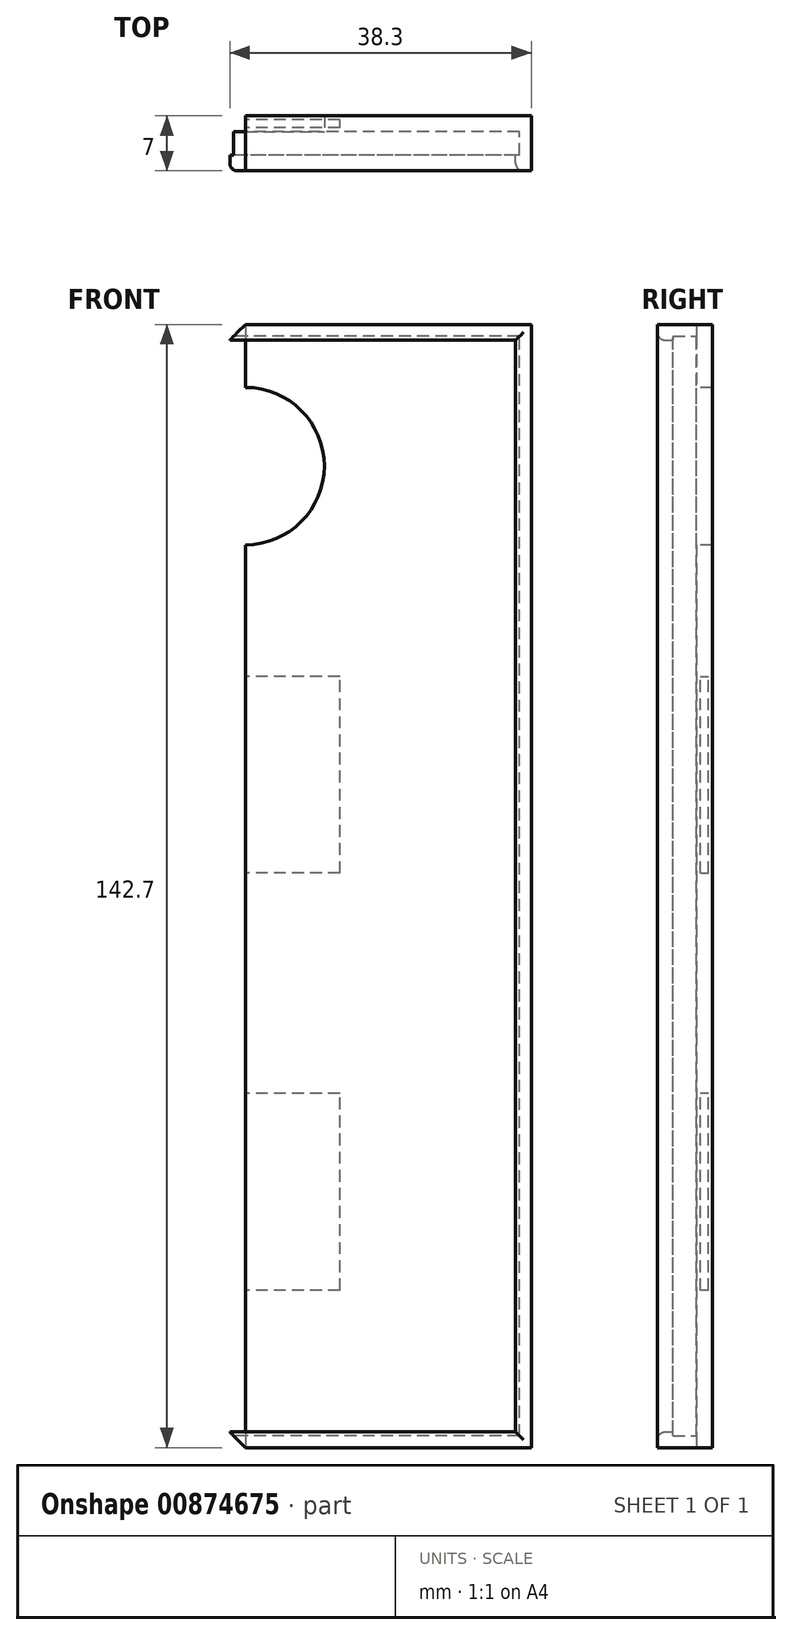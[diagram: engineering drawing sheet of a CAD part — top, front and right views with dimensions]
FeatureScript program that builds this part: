
annotation { "Feature Type Name" : "Feature", "Feature Type Description" : "" }
export const myFeature = defineFeature(function(context is Context, id is Id, definition is map)
    precondition{}
    {
        {
            var Q0;
            Q0=qCreatedBy(makeId("Right.planeOp"),FACE);
            var sketch = newSketch(context, id + "F0", { "sketchPlane" : qUnion([Q0])});
            skLineSegment(sketch, "E0.bottom", {"start": v(0.5, 132.36) * mm, "end": v(-1.5, 132.36) * mm});
            skLineSegment(sketch, "E0.top", {"start": v(0.5, -10.34) * mm, "end": v(-1.5, -10.34) * mm});
            skLineSegment(sketch, "E0.left", {"start": v(0.5, 132.36) * mm, "end": v(0.5, -10.34) * mm});
            skLineSegment(sketch, "E0.right", {"start": v(-1.5, 132.36) * mm, "end": v(-1.5, -10.34) * mm});
            skLineSegment(sketch, "E1.bottom", {"start": v(-0.5, -10.34) * mm, "end": v(-0.5, -10.34) * mm});
            skLineSegment(sketch, "E1.top", {"start": v(-0.5, 132.36) * mm, "end": v(-0.5, 132.36) * mm});
            skLineSegment(sketch, "E1.left", {"start": v(-0.5, -10.34) * mm, "end": v(-0.5, 132.36) * mm});
            skLineSegment(sketch, "E1.right", {"start": v(-0.5, -10.34) * mm, "end": v(-0.5, 132.36) * mm});
            skLineSegment(sketch, "E2.bottom", {"start": v(0, 34.66) * mm, "end": v(-1, 34.66) * mm});
            skLineSegment(sketch, "E2.top", {"start": v(0, 9.66) * mm, "end": v(-1, 9.66) * mm});
            skLineSegment(sketch, "E2.left", {"start": v(0, 9.66) * mm, "end": v(0, 34.66) * mm});
            skLineSegment(sketch, "E2.right", {"start": v(-1, 9.66) * mm, "end": v(-1, 34.66) * mm});
            skLineSegment(sketch, "E3.bottom", {"start": v(-1, 87.66) * mm, "end": v(0, 87.66) * mm});
            skLineSegment(sketch, "E3.top", {"start": v(-1, 62.66) * mm, "end": v(0, 62.66) * mm});
            skLineSegment(sketch, "E3.left", {"start": v(-1, 62.66) * mm, "end": v(-1, 87.66) * mm});
            skLineSegment(sketch, "E3.right", {"start": v(0, 62.66) * mm, "end": v(0, 87.66) * mm});
            skSolve(sketch);
        }
        {
            var Q0;
            Q0 = qSketchRegion(id + "F0", true);
            extrude(context, id + "F1", {"entities" : qUnion([Q0]), "endBound" : BoundingType.SYMMETRIC, "depth" : 12 * mm, "offsetDistance" : 25 * mm});
        }
        {
            var Q0;
            Q0=makeQuery(id+"F1.opExtrude","CAP_FACE",FACE,{"disambiguationData":[OSD([sQuery(id+"F0.wireOp",EDGE,"E0.bottom"),sQuery(id+"F0.wireOp",EDGE,"E0.top"),sQuery(id+"F0.wireOp",EDGE,"E0.left"),sQuery(id+"F0.wireOp",EDGE,"E0.right"),sQuery(id+"F0.wireOp",EDGE,"E2.bottom"),sQuery(id+"F0.wireOp",EDGE,"E2.top"),sQuery(id+"F0.wireOp",EDGE,"E2.left"),sQuery(id+"F0.wireOp",EDGE,"E2.right"),sQuery(id+"F0.wireOp",EDGE,"E3.bottom"),sQuery(id+"F0.wireOp",EDGE,"E3.top"),sQuery(id+"F0.wireOp",EDGE,"E3.left"),sQuery(id+"F0.wireOp",EDGE,"E3.right")])],"isStart":false});
            var sketch = newSketch(context, id + "F2", { "sketchPlane" : qUnion([Q0])});
            skLineSegment(sketch, "E4.bottom", {"start": v(-1.5, 132.36) * mm, "end": v(0.5, 132.36) * mm});
            skLineSegment(sketch, "E4.top", {"start": v(-1.5, -10.34) * mm, "end": v(0.5, -10.34) * mm});
            skLineSegment(sketch, "E4.left", {"start": v(-1.5, 132.36) * mm, "end": v(-1.5, -10.34) * mm});
            skLineSegment(sketch, "E4.right", {"start": v(0.5, 132.36) * mm, "end": v(0.5, -10.34) * mm});
            skSolve(sketch);
        }
        {
            var Q0;
            Q0 = qSketchRegion(id + "F2", true);
            extrude(context, id + "F3", {"entities" : qUnion([Q0]), "operationType" : NewBodyOperationType.ADD, "depth" : 24.3 * mm, "offsetDistance" : 25 * mm});
        }
        {
            var Q0;
            Q0=makeQuery(id+"F3.boolean.opBoolean","MERGE",FACE,{"derivedFrom":[makeQuery(id+"F1.opExtrude","SWEPT_FACE",FACE,{"disambiguationData":[OSD([sQuery(id+"F0.wireOp",EDGE,"E0.right")])]}),makeQuery(id+"F3.opExtrude","SWEPT_FACE",FACE,{"disambiguationData":[OSD([sQuery(id+"F2.wireOp",EDGE,"E4.left")])]})]});
            var sketch = newSketch(context, id + "F4", { "sketchPlane" : qUnion([Q0])});
            skCircle(sketch, "E5", {"center": v(-6, 114.36) * mm, "radius": 10 * mm});
            skSolve(sketch);
        }
        {
            var Q0;
            Q0=sQuery(id+"F4.wireOp",VERTEX,"E5.center");
            var Q1;
            Q1=makeQuery(id+"F1.opExtrude","SWEPT_BODY",BODY,{"disambiguationData":[OSD([sQuery(id+"F0.wireOp",EDGE,"E0.bottom"),sQuery(id+"F0.wireOp",EDGE,"E0.top"),sQuery(id+"F0.wireOp",EDGE,"E0.left"),sQuery(id+"F0.wireOp",EDGE,"E0.right"),sQuery(id+"F0.wireOp",EDGE,"E2.bottom"),sQuery(id+"F0.wireOp",EDGE,"E2.top"),sQuery(id+"F0.wireOp",EDGE,"E2.left"),sQuery(id+"F0.wireOp",EDGE,"E2.right"),sQuery(id+"F0.wireOp",EDGE,"E3.bottom"),sQuery(id+"F0.wireOp",EDGE,"E3.top"),sQuery(id+"F0.wireOp",EDGE,"E3.left"),sQuery(id+"F0.wireOp",EDGE,"E3.right")])]});
            hole(context, id + "F5", {"style" : HoleStyle.SIMPLE, "endStyle" : HoleEndStyle.THROUGH, "holeDiameter" : 20 * mm, "majorDiameter" : 5 * mm, "isTappedThrough" : true, "tappedDepth" : 12 * mm, "tapClearance" : 3, "locations" : qUnion([Q0]), "scope" : qUnion([Q1])});
        }
        {
            var Q0;
            Q0=makeQuery(id+"F3.boolean.opBoolean","MERGE",FACE,{"derivedFrom":[makeQuery(id+"F1.opExtrude","SWEPT_FACE",FACE,{"disambiguationData":[OSD([sQuery(id+"F0.wireOp",EDGE,"E0.right")])]}),makeQuery(id+"F3.opExtrude","SWEPT_FACE",FACE,{"disambiguationData":[OSD([sQuery(id+"F2.wireOp",EDGE,"E4.left")])]})]});
            var sketch = newSketch(context, id + "F6", { "sketchPlane" : qUnion([Q0])});
            skLineSegment(sketch, "E6", {"start": v(-6, 132.36) * mm, "end": v(30.3, 132.36) * mm});
            skLineSegment(sketch, "E7", {"start": v(30.3, 132.36) * mm, "end": v(30.3, -10.34) * mm});
            skLineSegment(sketch, "E8", {"start": v(30.3, -10.34) * mm, "end": v(-6, -10.34) * mm});
            skLineSegment(sketch, "E9", {"start": v(28.8, -8.84) * mm, "end": v(28.8, 130.86) * mm});
            skLineSegment(sketch, "E10", {"start": v(-6, -10.34) * mm, "end": v(-7.5, -8.84) * mm});
            skLineSegment(sketch, "E11", {"start": v(28.8, -8.84) * mm, "end": v(-7.5, -8.84) * mm});
            skLineSegment(sketch, "E12", {"start": v(-6, 132.36) * mm, "end": v(-7.5, 130.86) * mm});
            skLineSegment(sketch, "E13", {"start": v(28.8, 130.86) * mm, "end": v(-7.5, 130.86) * mm});
            skSolve(sketch);
        }
        {
            var Q0;
            Q0 = qSketchRegion(id + "F6", true);
            extrude(context, id + "F7", {"entities" : qUnion([Q0]), "operationType" : NewBodyOperationType.ADD, "depth" : 3 * mm, "offsetDistance" : 25 * mm});
        }
        {
            var Q0;
            Q0=makeQuery(id+"F7.opExtrude","CAP_FACE",FACE,{"disambiguationData":[OSD([sQuery(id+"F6.wireOp",EDGE,"E6"),sQuery(id+"F6.wireOp",EDGE,"E7"),sQuery(id+"F6.wireOp",EDGE,"E8"),sQuery(id+"F6.wireOp",EDGE,"E9"),sQuery(id+"F6.wireOp",EDGE,"E10"),sQuery(id+"F6.wireOp",EDGE,"E11"),sQuery(id+"F6.wireOp",EDGE,"E12"),sQuery(id+"F6.wireOp",EDGE,"E13")])],"isStart":false});
            var sketch = newSketch(context, id + "F8", { "sketchPlane" : qUnion([Q0])});
            skLineSegment(sketch, "E14", {"start": v(30.3, -10.34) * mm, "end": v(-6, -10.34) * mm});
            skLineSegment(sketch, "E15", {"start": v(-6, -10.34) * mm, "end": v(-8, -8.34) * mm});
            skLineSegment(sketch, "E16", {"start": v(30.3, -10.34) * mm, "end": v(30.3, 132.36) * mm});
            skLineSegment(sketch, "E17", {"start": v(30.3, 132.36) * mm, "end": v(-6, 132.36) * mm});
            skLineSegment(sketch, "E18", {"start": v(-6, 132.36) * mm, "end": v(-8, 130.36) * mm});
            skLineSegment(sketch, "E19", {"start": v(28.3, -8.34) * mm, "end": v(28.3, 130.36) * mm});
            skLineSegment(sketch, "E20", {"start": v(28.3, -8.34) * mm, "end": v(-8, -8.34) * mm});
            skLineSegment(sketch, "E21", {"start": v(28.3, 130.36) * mm, "end": v(-8, 130.36) * mm});
            skSolve(sketch);
        }
        {
            var Q0;
            Q0 = qSketchRegion(id + "F8", true);
            extrude(context, id + "F9", {"entities" : qUnion([Q0]), "operationType" : NewBodyOperationType.ADD, "depth" : 2 * mm, "offsetDistance" : 25 * mm});
        }
        {
            var Q0;
            Q0=makeQuery(id+"F9.opExtrude","CAP_EDGE",EDGE,{"disambiguationData":[OSD([sQuery(id+"F8.wireOp",EDGE,"E20")])],"isStart":false});
            var Q1;
            Q1=makeQuery(id+"F9.opExtrude","CAP_EDGE",EDGE,{"disambiguationData":[OSD([sQuery(id+"F8.wireOp",EDGE,"E19")])],"isStart":false});
            var Q2;
            Q2=makeQuery(id+"F9.opExtrude","CAP_EDGE",EDGE,{"disambiguationData":[OSD([sQuery(id+"F8.wireOp",EDGE,"E21")])],"isStart":false});
            fillet(context, id + "F10", {"entities" : qUnion([Q0, Q1, Q2]), "radius" : 1 * mm, "tangentPropagation" : true, "allowEdgeOverflow" : false});
        }
    });
